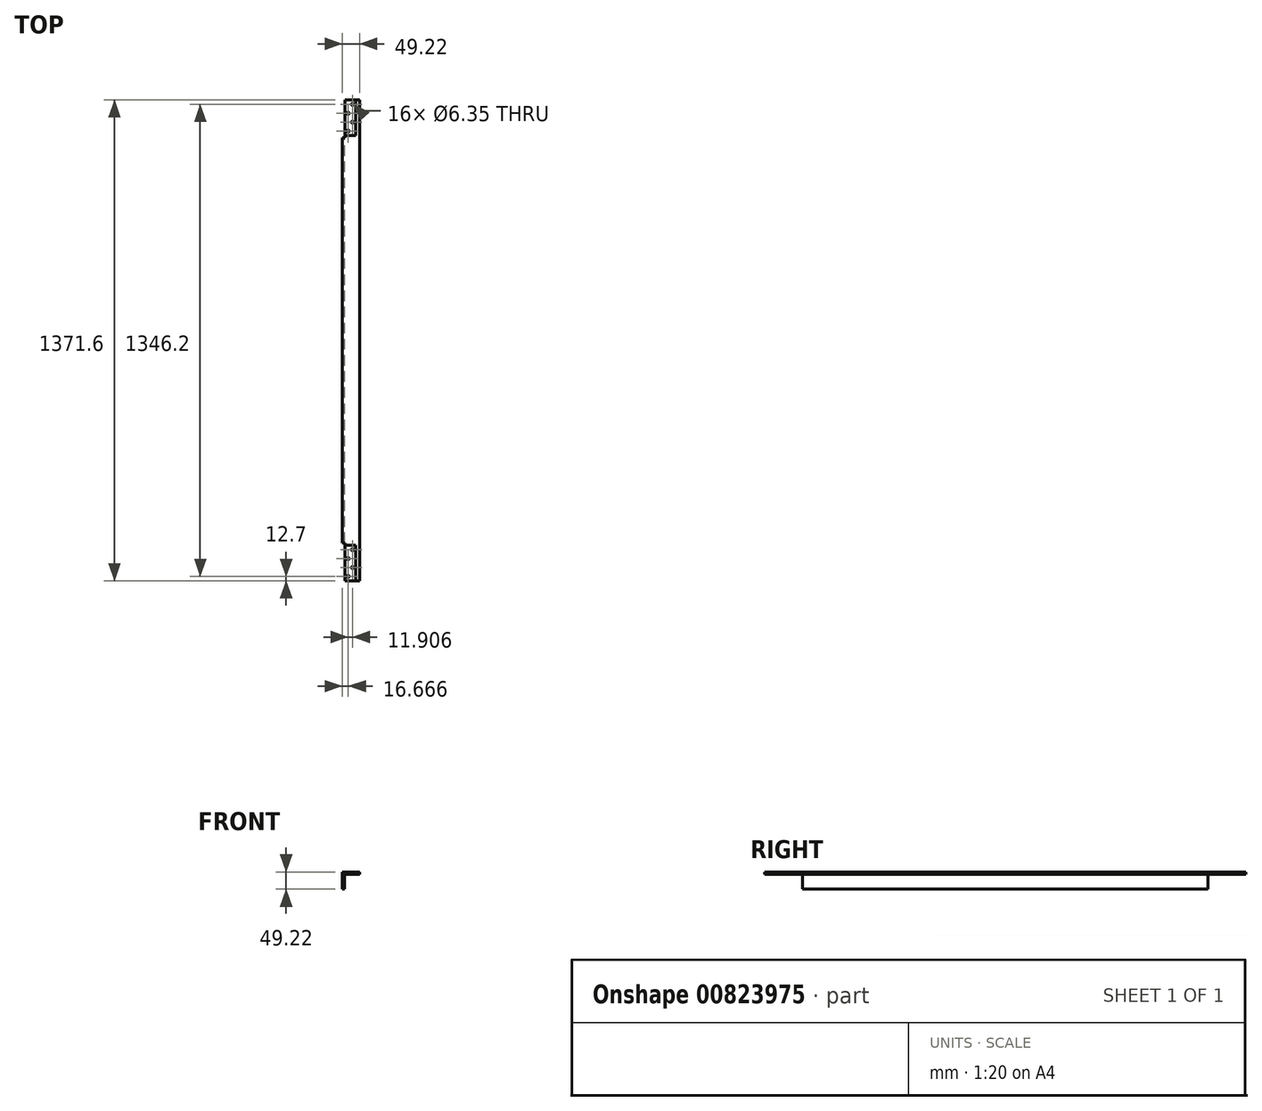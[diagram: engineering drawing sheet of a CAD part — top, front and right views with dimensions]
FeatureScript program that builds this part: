
annotation { "Feature Type Name" : "Feature", "Feature Type Description" : "" }
export const myFeature = defineFeature(function(context is Context, id is Id, definition is map)
    precondition{}
    {
        {
            var Q0;
            Q0=qCreatedBy(makeId("Front.planeOp"),FACE);
            var sketch = newSketch(context, id + "F0", { "sketchPlane" : qUnion([Q0])});
            skLineSegment(sketch, "E0.bottom", {"start": v(-18.26, -24.61) * mm, "end": v(-24.61, -24.61) * mm});
            skLineSegment(sketch, "E0.top", {"start": v(24.61, 24.61) * mm, "end": v(-24.61, 24.61) * mm});
            skLineSegment(sketch, "E0.left", {"start": v(24.61, 18.26) * mm, "end": v(24.61, 24.61) * mm});
            skLineSegment(sketch, "E0.right", {"start": v(-24.61, -24.61) * mm, "end": v(-24.61, 24.61) * mm});
            skPoint(sketch, "E0.middle", {"position": v(0, 0) * mm});
            skLineSegment(sketch, "E1", {"start": v(-18.26, -24.61) * mm, "end": v(-18.26, 18.26) * mm});
            skLineSegment(sketch, "E2", {"start": v(-18.26, 18.26) * mm, "end": v(24.61, 18.26) * mm});
            skSolve(sketch);
        }
        {
            var Q0;
            Q0=makeQuery(id+"F0.imprint","IMPRINT",FACE,{"disambiguationData":[TD([[makeQuery(id+"F0.imprint","IMPRINT",EDGE,{"derivedFrom":sQuery(id+"F0.wireOp",EDGE,"E0.bottom")}),-1.0]])]});
            extrude(context, id + "F1", {"entities" : qUnion([Q0]), "endBound" : BoundingType.SYMMETRIC, "depth" : 1371.6 * mm, "offsetDistance" : 25.4 * mm});
        }
        {
            var Q0;
            Q0=makeQuery(id+"F1.opExtrude","SWEPT_FACE",FACE,{"disambiguationData":[OSD([sQuery(id+"F0.wireOp",EDGE,"E0.top")])]});
            var sketch = newSketch(context, id + "F2", { "sketchPlane" : qUnion([Q0])});
            skLineSegment(sketch, "E3.bottom", {"start": v(-24.61, -685.8) * mm, "end": v(-17.47, -685.8) * mm});
            skLineSegment(sketch, "E3.top", {"start": v(-24.61, -577.85) * mm, "end": v(-17.47, -577.85) * mm});
            skLineSegment(sketch, "E3.left", {"start": v(-24.61, -685.8) * mm, "end": v(-24.61, -577.85) * mm});
            skLineSegment(sketch, "E3.right", {"start": v(-17.47, -685.8) * mm, "end": v(-17.47, -584.2) * mm});
            skLineSegment(sketch, "E4.bottom", {"start": v(-17.47, -685.8) * mm, "end": v(13.49, -685.8) * mm});
            skLineSegment(sketch, "E4.top", {"start": v(-17.47, -584.2) * mm, "end": v(13.49, -584.2) * mm});
            skLineSegment(sketch, "E4.right", {"start": v(13.49, -685.8) * mm, "end": v(13.49, -584.2) * mm});
            skLineSegment(sketch, "E5", {"start": v(-17.47, -577.85) * mm, "end": v(-17.47, -584.2) * mm});
            skCircle(sketch, "E6", {"center": v(-7.94, -673.1) * mm, "radius": 3.18 * mm});
            skCircle(sketch, "E7", {"center": v(-7.94, -622.3) * mm, "radius": 3.18 * mm});
            skCircle(sketch, "E8", {"center": v(3.96, -647.7) * mm, "radius": 3.18 * mm});
            skCircle(sketch, "E9", {"center": v(3.96, -596.9) * mm, "radius": 3.18 * mm});
            skLineSegment(sketch, "E10.bottom", {"start": v(-24.61, 685.8) * mm, "end": v(-17.47, 685.8) * mm});
            skLineSegment(sketch, "E10.top", {"start": v(-24.61, 577.85) * mm, "end": v(-17.47, 577.85) * mm});
            skLineSegment(sketch, "E10.left", {"start": v(-24.61, 685.8) * mm, "end": v(-24.61, 577.85) * mm});
            skLineSegment(sketch, "E10.right", {"start": v(-17.47, 685.8) * mm, "end": v(-17.47, 577.85) * mm});
            skLineSegment(sketch, "E11.bottom", {"start": v(-17.47, 584.2) * mm, "end": v(13.49, 584.2) * mm});
            skLineSegment(sketch, "E11.top", {"start": v(-17.47, 685.8) * mm, "end": v(13.49, 685.8) * mm});
            skLineSegment(sketch, "E11.left", {"start": v(-17.47, 584.2) * mm, "end": v(-17.47, 685.8) * mm});
            skLineSegment(sketch, "E11.right", {"start": v(13.49, 584.2) * mm, "end": v(13.49, 685.8) * mm});
            skCircle(sketch, "E12", {"center": v(-7.94, 647.7) * mm, "radius": 3.18 * mm});
            skCircle(sketch, "E13", {"center": v(-7.94, 596.9) * mm, "radius": 3.18 * mm});
            skCircle(sketch, "E14", {"center": v(3.96, 622.3) * mm, "radius": 3.18 * mm});
            skCircle(sketch, "E15", {"center": v(3.96, 673.1) * mm, "radius": 3.18 * mm});
            skSolve(sketch);
        }
        {
            var Q0;
            Q0=makeQuery(id+"F2.imprint","IMPRINT",FACE,{"disambiguationData":[TD([[makeQuery(id+"F2.imprint","IMPRINT",EDGE,{"derivedFrom":sQuery(id+"F2.wireOp",EDGE,"E4.bottom")}),-1.0]])]});
            var Q1;
            Q1=makeQuery(id+"F2.imprint","IMPRINT",FACE,{"disambiguationData":[TD([[makeQuery(id+"F2.imprint","IMPRINT",EDGE,{"derivedFrom":sQuery(id+"F2.wireOp",EDGE,"E11.bottom")}),1.0]])]});
            extrude(context, id + "F3", {"entities" : qUnion([Q0, Q1]), "operationType" : NewBodyOperationType.REMOVE, "oppositeDirection" : true, "depth" : 3.17 * mm, "offsetDistance" : 25.4 * mm});
        }
        {
            var Q0;
            Q0=makeQuery(id+"F2.imprint","IMPRINT",FACE,{"disambiguationData":[TD([[makeQuery(id+"F2.imprint","IMPRINT",EDGE,{"derivedFrom":sQuery(id+"F2.wireOp",EDGE,"E10.bottom")}),1.0]])]});
            var Q1;
            Q1=makeQuery(id+"F2.imprint","IMPRINT",FACE,{"disambiguationData":[TD([[makeQuery(id+"F2.imprint","IMPRINT",EDGE,{"derivedFrom":sQuery(id+"F2.wireOp",EDGE,"E3.bottom")}),-1.0]])]});
            extrude(context, id + "F4", {"entities" : qUnion([Q0, Q1]), "operationType" : NewBodyOperationType.REMOVE, "endBound" : BoundingType.THROUGH_ALL, "oppositeDirection" : true, "depth" : 25.4 * mm, "offsetDistance" : 25.4 * mm});
        }
        {
            var Q0;
            Q0=sQuery(id+"F2.wireOp",VERTEX,"E6.center");
            var Q1;
            Q1=sQuery(id+"F2.wireOp",VERTEX,"E8.center");
            var Q2;
            Q2=sQuery(id+"F2.wireOp",VERTEX,"E7.center");
            var Q3;
            Q3=sQuery(id+"F2.wireOp",VERTEX,"E9.center");
            var Q4;
            Q4=sQuery(id+"F2.wireOp",VERTEX,"E12.center");
            var Q5;
            Q5=sQuery(id+"F2.wireOp",VERTEX,"E15.center");
            var Q6;
            Q6=sQuery(id+"F2.wireOp",VERTEX,"E14.center");
            var Q7;
            Q7=sQuery(id+"F2.wireOp",VERTEX,"E13.center");
            var Q8;
            Q8=makeQuery(id+"F1.opExtrude","SWEPT_BODY",BODY,{"disambiguationData":[OSD([sQuery(id+"F0.wireOp",EDGE,"E0.bottom"),sQuery(id+"F0.wireOp",EDGE,"E0.top"),sQuery(id+"F0.wireOp",EDGE,"E0.left"),sQuery(id+"F0.wireOp",EDGE,"E0.right"),sQuery(id+"F0.wireOp",EDGE,"E1"),sQuery(id+"F0.wireOp",EDGE,"E2")])]});
            hole(context, id + "F5", {"style" : HoleStyle.SIMPLE, "endStyle" : HoleEndStyle.THROUGH, "holeDiameter" : 6.35 * mm, "majorDiameter" : 6.35 * mm, "isTappedThrough" : true, "tappedDepth" : 12.7 * mm, "tapClearance" : 3, "locations" : qUnion([Q0, Q1, Q2, Q3, Q4, Q5, Q6, Q7]), "scope" : qUnion([Q8])});
        }
    });
